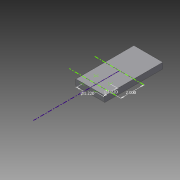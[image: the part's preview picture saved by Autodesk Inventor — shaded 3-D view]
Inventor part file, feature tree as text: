
AUTODESK INVENTOR PART (.ipt)
format: ipt  version: 2015 (Build 190159000, 159)  size: 80,384 bytes
history: native  units: in
note: dims shown in document units (in); Inventor stores cm internally (conversion verified against a paired STEP export)
features: sketch x2, extrude x1
ambient origin geometry x8: Origin, YZ Plane, XZ Plane, XY Plane, X Axis, Y Axis, Z Axis, Center Point
bodies: Solid1 (feature_tree)
feature tree (3):
  extrude  "Extrusion1"  Depth=5.0in
  sketch  "Sketch2"  dims[d2=0.5in d3=0.0in d6=2.0in d7=1.2205in d8=1.22in]
  sketch  "Sketch1"  dims[d0=2.5in d1=5.0in]
